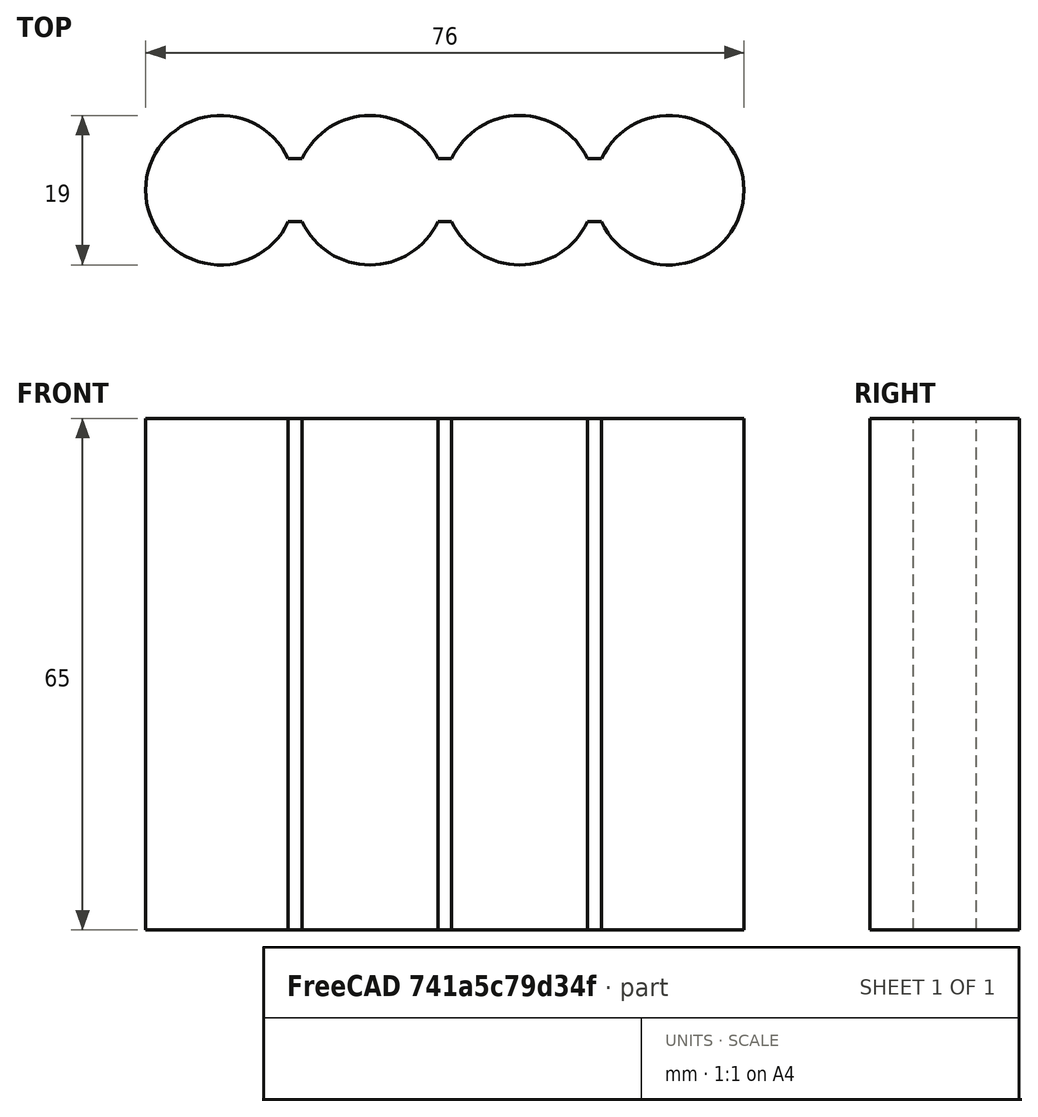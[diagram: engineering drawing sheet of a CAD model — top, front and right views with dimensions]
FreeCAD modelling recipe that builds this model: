
FCSTD DOCUMENT
Label: CellDummy
objects: Sketcher::SketchObject×1, PartDesign::Pad×1
note: 3 computed .brp shape members not serialized (recipe doc carries the construction recipe); baked Part::Feature solids carry a one-line shape summary decoded from their .brp

FEATURE [Sketcher::SketchObject] Sketch
  sketch-geometry (19):
    g0: ArcOfCircle CenterX=9.5 CenterY=9.5 CenterZ=0 NormalX=0 NormalY=0 NormalZ=1 Radius=9.5 StartAngle=0.434606 EndAngle=5.84858
    g1: ArcOfCircle CenterX=28.5 CenterY=9.5 CenterZ=0 NormalX=0 NormalY=0 NormalZ=1 Radius=9.5 StartAngle=0.434606 EndAngle=2.70699
    g2: ArcOfCircle CenterX=47.5 CenterY=9.5 CenterZ=0 NormalX=0 NormalY=0 NormalZ=1 Radius=9.5 StartAngle=0.434606 EndAngle=2.70699
    g3: ArcOfCircle CenterX=66.5 CenterY=9.5 CenterZ=0 NormalX=0 NormalY=0 NormalZ=1 Radius=9.5 StartAngle=3.5762 EndAngle=8.99017
    g4: ArcOfCircle CenterX=47.5 CenterY=9.5 CenterZ=0 NormalX=0 NormalY=0 NormalZ=1 Radius=9.5 StartAngle=3.5762 EndAngle=5.84858
    g5: ArcOfCircle CenterX=28.5 CenterY=9.5 CenterZ=0 NormalX=0 NormalY=0 NormalZ=1 Radius=9.5 StartAngle=3.5762 EndAngle=5.84858
    g6: LineSegment StartX=18.1168 StartY=5.5 StartZ=0 EndX=19.8832 EndY=5.5 EndZ=0
    g7: LineSegment [constr] StartX=19.8832 StartY=5.5 StartZ=0 EndX=37.1168 EndY=5.5 EndZ=0
    g8: LineSegment StartX=37.1168 StartY=5.5 StartZ=0 EndX=38.8832 EndY=5.5 EndZ=0
    g9: LineSegment [constr] StartX=38.8832 StartY=5.5 StartZ=0 EndX=56.1168 EndY=5.5 EndZ=0
    g10: LineSegment StartX=56.1168 StartY=5.5 StartZ=0 EndX=57.8832 EndY=5.5 EndZ=0
    g11: LineSegment StartX=57.8832 StartY=13.5 StartZ=0 EndX=56.1168 EndY=13.5 EndZ=0
    g12: LineSegment [constr] StartX=56.1168 StartY=13.5 StartZ=0 EndX=38.8832 EndY=13.5 EndZ=0
    g13: LineSegment StartX=38.8832 StartY=13.5 StartZ=0 EndX=37.1168 EndY=13.5 EndZ=0
    g14: LineSegment [constr] StartX=37.1168 StartY=13.5 StartZ=0 EndX=19.8832 EndY=13.5 EndZ=0
    g15: LineSegment StartX=19.8832 StartY=13.5 StartZ=0 EndX=18.1168 EndY=13.5 EndZ=0
    g16: LineSegment [constr] StartX=9.5 StartY=9.5 StartZ=0 EndX=28.5 EndY=9.5 EndZ=0
    g17: LineSegment [constr] StartX=28.5 StartY=9.5 StartZ=0 EndX=47.5 EndY=9.5 EndZ=0
    g18: LineSegment [constr] StartX=47.5 StartY=9.5 StartZ=0 EndX=66.5 EndY=9.5 EndZ=0
  constraints (54):
    c: Coincident(g6,g0)
    c: Coincident(g6,g5)
    c: Coincident(g6,g7)
    c: Coincident(g7,g5)
    c: Coincident(g7,g8)
    c: Coincident(g8,g4)
    c: Coincident(g8,g9)
    c: Coincident(g9,g4)
    c: Coincident(g9,g10)
    c: Coincident(g10,g3)
    c: Coincident(g11,g12)
    c: Coincident(g12,g2)
    c: Horizontal(g12)
    c: Coincident(g12,g13)
    c: Coincident(g13,g1)
    c: Coincident(g13,g14)
    c: Coincident(g14,g1)
    c: Coincident(g14,g15)
    c: Coincident(g15,g0)
    c: Horizontal(g10)
    c: Horizontal(g9)
    c: Horizontal(g8)
    c: Horizontal(g7)
    c: Horizontal(g6)
    c: Horizontal(g15)
    c: Horizontal(g14)
    c: Horizontal(g13)
    c: Horizontal(g11)
    c: Coincident(g11,g2)
    c: Coincident(g11,g3)
    c: Equal(g0,g1)
    c: Equal(g1,g2)
    c: Equal(g2,g3)
    c: Equal(g3,g4)
    c: Equal(g4,g5)
    c: Coincident(g1,g5)
    c: Coincident(g2,g4)
    c: Coincident(g16,g0)
    c: Coincident(g16,g1)
    c: Horizontal(g16)
    c: Coincident(g16,g17)
    c: Coincident(g17,g2)
    c: Coincident(g17,g18)
    c: Coincident(g18,g3)
    c: Horizontal(g18)
    c: Horizontal(g17)
    c: Equal(g16,g17)
    c: Equal(g17,g18)
    c: Radius(g0) = 9.5
    c: DistanceX(g16) = 19
    c: DistanceY(g3,g3) = -4
    c: DistanceY(g3,g3) = 4
    c: DistanceX(g0) = 9.5
    c: DistanceY(g0) = 9.5
FEATURE [PartDesign::Pad] Pad
  Length = 65
  MirroredExtent = false
  Sketch = -> Sketch
